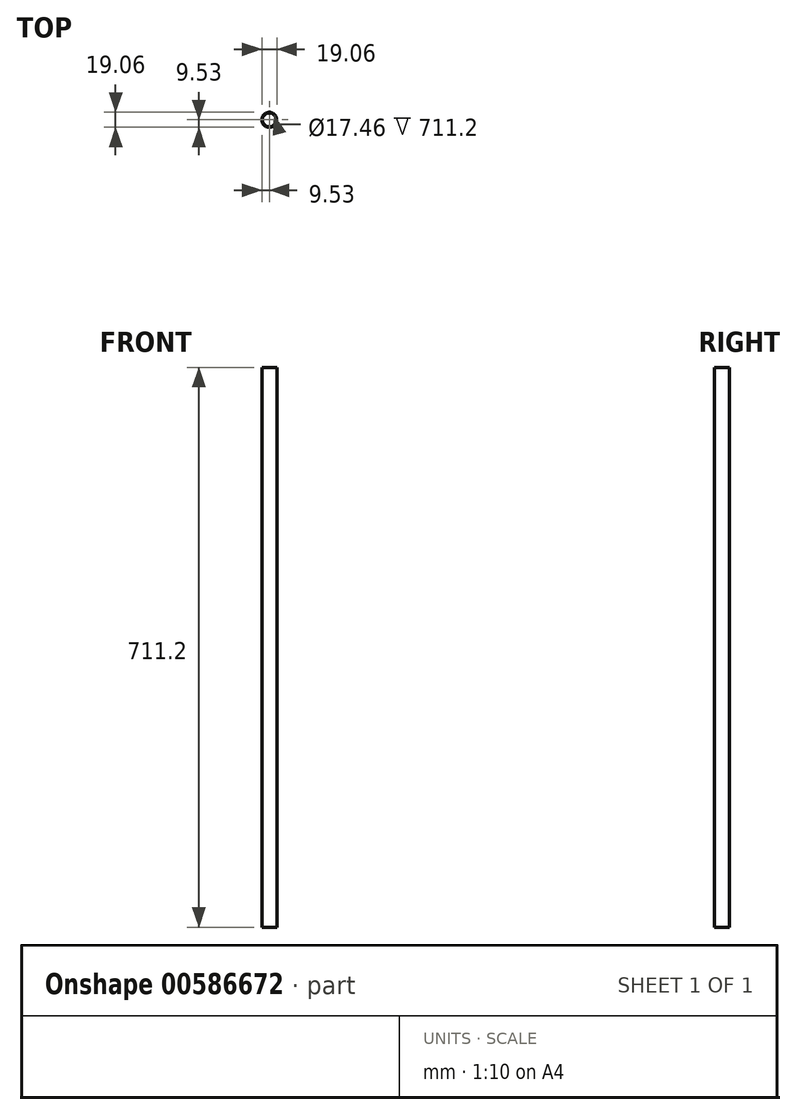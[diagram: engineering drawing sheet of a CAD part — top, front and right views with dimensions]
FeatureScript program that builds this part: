
annotation { "Feature Type Name" : "Feature", "Feature Type Description" : "" }
export const myFeature = defineFeature(function(context is Context, id is Id, definition is map)
    precondition{}
    {
        {
            var Q0;
            Q0=qCreatedBy(makeId("Top.planeOp"),FACE);
            var sketch = newSketch(context, id + "F0", { "sketchPlane" : qUnion([Q0])});
            skCircle(sketch, "E0", {"center": v(0, 0) * mm, "radius": 9.53 * mm});
            skCircle(sketch, "E1.0", {"center": v(0, 0) * mm, "radius": 8.73 * mm});
            skSolve(sketch);
        }
        {
            var Q0;
            Q0 = qSketchRegion(id + "F0", true);
            extrude(context, id + "F1", {"entities" : qUnion([Q0]), "endBound" : BoundingType.SYMMETRIC, "depth" : 711.2 * mm, "offsetDistance" : 25.4 * mm});
        }
    });
